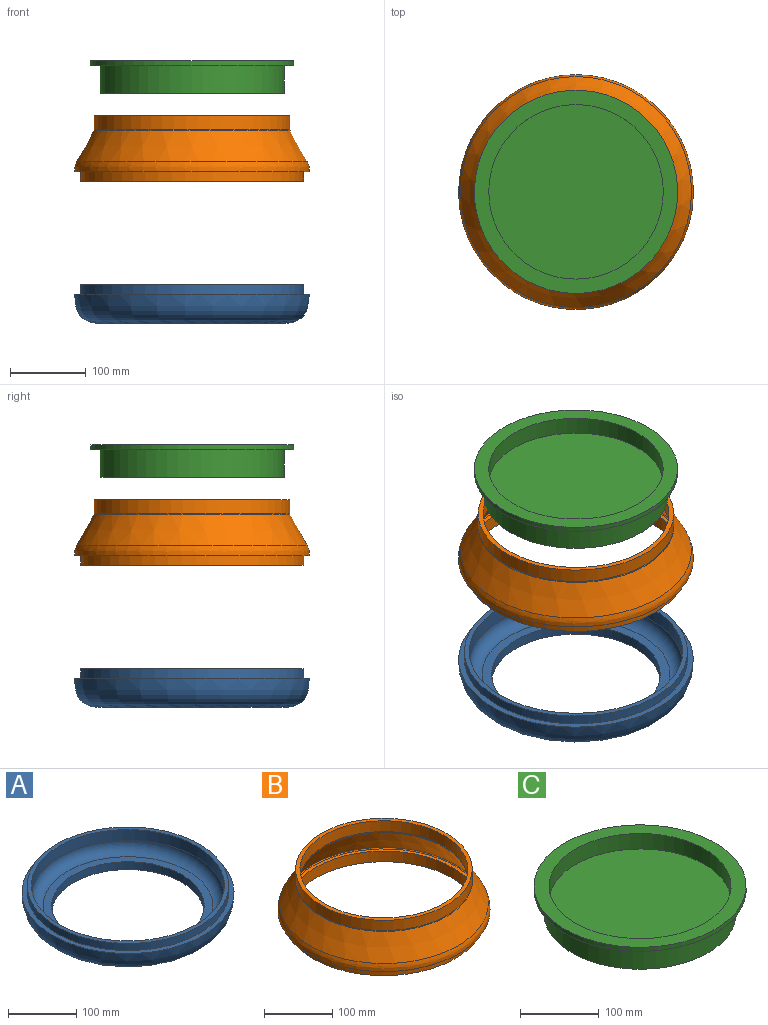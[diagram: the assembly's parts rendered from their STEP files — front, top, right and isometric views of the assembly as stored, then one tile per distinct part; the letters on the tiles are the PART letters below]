
ASSEMBLY  parts=3 mates=2
PART A: 9 faces, bbox 310.9x310.9x50.8 mm
  f0: cylinder r=111.76mm len=223.52mm, axis (0,0,-1), area 9809.9mm2, adj f1,f8
  f1: plane 248.92x248.92mm, normal (0,0,1), area 9424.8mm2, adj f0,f2
  f2: torus R=124.46mm, axis (0,0,-1), area 22724.1mm2, adj f1,f3
  f3: cylinder r=141.48mm len=282.96mm, axis (0,0,-1), area 17611.5mm2, adj f2,f4
  f4: plane 295.66x295.66mm, normal (0,0,1), area 5771.4mm2, adj f3,f5
  f5: cylinder r=147.83mm len=295.66mm, axis (0,0,-1), area 11796.2mm2, adj f4,f6
  f6: plane 310.9x310.9mm, normal (0,0,1), area 7260.1mm2, adj f5,f7
  f7: revolved ~310.9x310.9mm, area 51614.5mm2, adj f6,f8
  f8: plane 248.92x248.92mm, normal (0,0,-1), area 9424.8mm2, adj f0,f7
PART B: 14 faces, bbox 321x321x86.4 mm
  f0: revolved ~311.01x311.01mm, area 12774.8mm2, adj f1,f13
  f1: cone r=129.86mm half-angle=29.1deg, axis (0,0,-1), area 42040.3mm2, adj f0,f2
  f2: torus R=132.08mm, axis (0,0,-1), area 1052.4mm2, adj f1,f3
  f3: cylinder r=129.54mm len=259.08mm, axis (0,0,-1), area 14967.8mm2, adj f2,f4
  f4: plane 259.08x259.08mm, normal (0,0,1), area 5041.7mm2, adj f3,f5
  f5: cylinder r=123.19mm len=246.38mm, axis (0,0,-1), area 15000.7mm2, adj f4,f6
  f6: torus R=128.27mm, axis (0,0,-1), area 2003.5mm2, adj f5,f7
  f7: cone r=148.13mm half-angle=29.1deg, axis (0,0,-1), area 42618.5mm2, adj f6,f8
  f8: torus R=147.02mm, axis (0,0,-1), area 2454.5mm2, adj f7,f9
  f9: plane 294.03x294.03mm, normal (0,0,1), area 5019.3mm2, adj f8,f10
  f10: cylinder r=141.48mm len=282.96mm, axis (0,0,-1), area 16934.2mm2, adj f9,f11
  f11: plane 295.66x295.66mm, normal (0,0,-1), area 5771.4mm2, adj f10,f12
  f12: cylinder r=147.83mm len=295.66mm, axis (0,0,-1), area 11796.2mm2, adj f11,f13
  f13: plane 310.9x310.9mm, normal (0,0,-1), area 7260.1mm2, adj f0,f12
PART C: 10 faces, bbox 269.2x269.2x43.1 mm
  f0: plane 221.14x221.14mm, normal (0,0,-1), area 38408.2mm2, adj f9
  f1: cylinder r=115.57mm len=231.14mm, axis (0,0,1), area 5591.3mm2, adj f2,f9
  f2: plane 243.84x243.84mm, normal (0,0,-1), area 4737.7mm2, adj f1,f3
  f3: cylinder r=121.92mm len=243.84mm, axis (0,0,1), area 28116.2mm2, adj f2,f4
  f4: plane 269.24x269.24mm, normal (0,0,-1), area 10235.5mm2, adj f3,f5
  f5: cylinder r=134.62mm len=269.24mm, axis (0,0,1), area 5371.1mm2, adj f4,f6
  f6: plane 269.24x269.24mm, normal (0,0,1), area 14973.2mm2, adj f5,f7
  f7: cylinder r=115.57mm len=231.14mm, axis (0,0,1), area 17429.7mm2, adj f6,f8
  f8: plane 231.14x231.14mm, normal (0,0,1), area 41960.4mm2, adj f7
  f9: torus R=110.57mm, axis (0,0,1), area 5613.5mm2, adj f0,f1
PLACE A t=(81.38,-141.82,-189.34)mm
PLACE B t=(81.38,-141.82,11.46)mm
PLACE C t=(81.38,-141.82,127.82)mm
MATE revolute C.f9 <-> B.f3  axis (0,0,-1) through (81.38,-141.82,115.12)mm
MATE revolute B.f3 <-> A.f0  axis (0,0,-1) through (81.38,-141.82,5.11)mm
